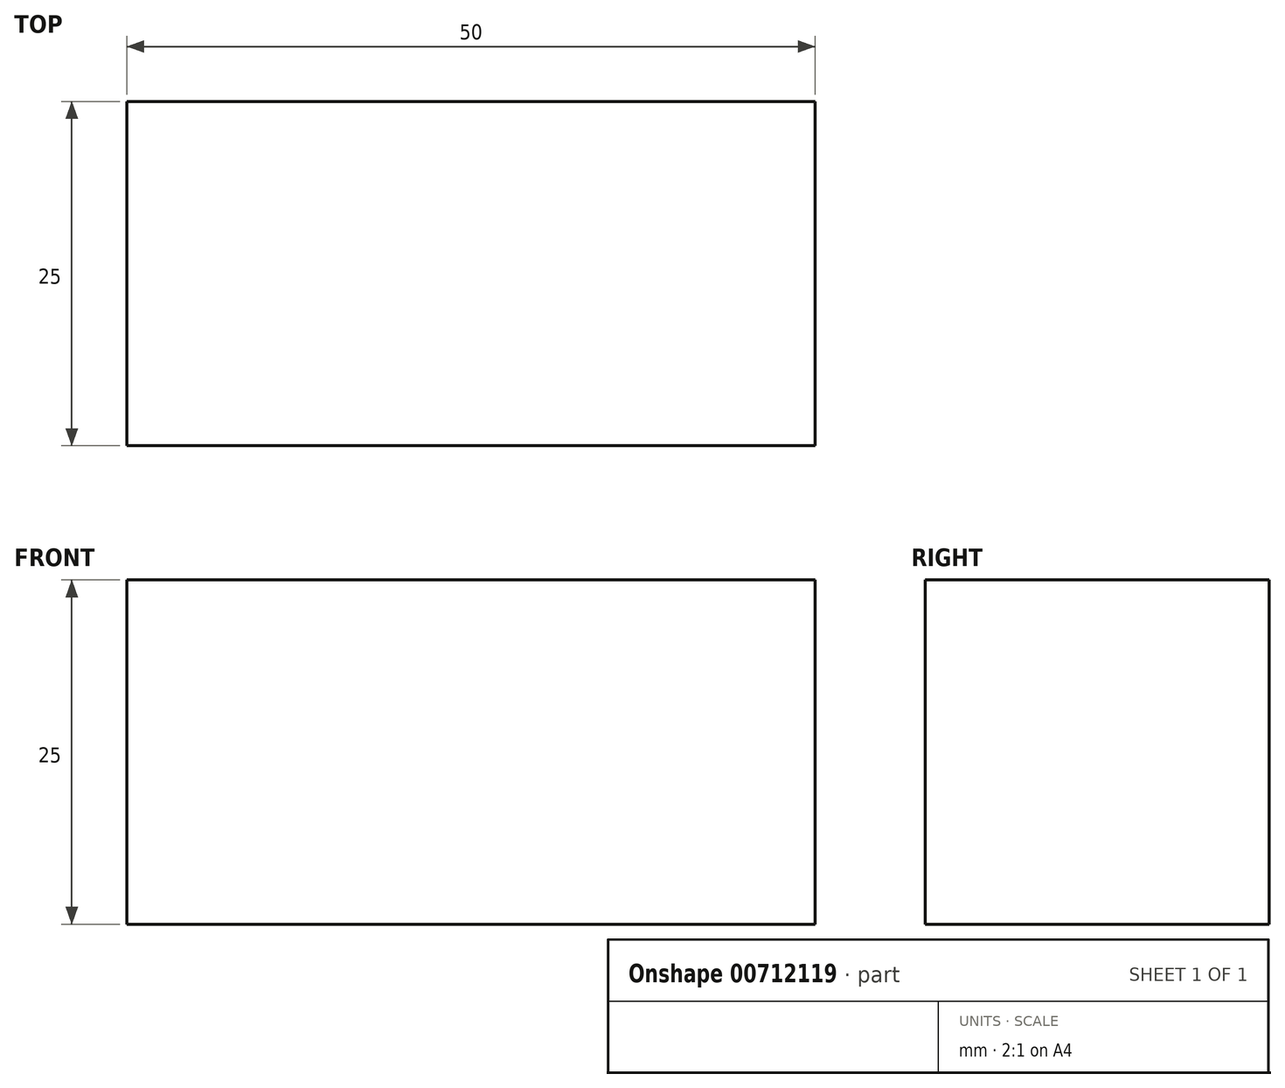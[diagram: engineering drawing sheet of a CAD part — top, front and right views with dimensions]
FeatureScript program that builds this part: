
annotation { "Feature Type Name" : "Feature", "Feature Type Description" : "" }
export const myFeature = defineFeature(function(context is Context, id is Id, definition is map)
    precondition{}
    {
        {
            var Q0;
            Q0=qCreatedBy(makeId("Top.planeOp"),FACE);
            var sketch = newSketch(context, id + "F0", { "sketchPlane" : qUnion([Q0])});
            skLineSegment(sketch, "E0.bottom", {"start": v(50, 25) * mm, "end": v(0, 25) * mm});
            skLineSegment(sketch, "E0.top", {"start": v(50, 0) * mm, "end": v(0, 0) * mm});
            skLineSegment(sketch, "E0.left", {"start": v(50, 25) * mm, "end": v(50, 0) * mm});
            skLineSegment(sketch, "E0.right", {"start": v(0, 25) * mm, "end": v(0, 0) * mm});
            skSolve(sketch);
        }
        {
            var Q0;
            Q0=makeQuery(id+"F0.imprint","IMPRINT",FACE,{"disambiguationData":[TD([[makeQuery(id+"F0.imprint","IMPRINT",EDGE,{"derivedFrom":sQuery(id+"F0.wireOp",EDGE,"E0.bottom")}),1.0]])]});
            extrude(context, id + "F1", {"entities" : qUnion([Q0]), "depth" : 25 * mm, "offsetDistance" : 25 * mm});
        }
    });
